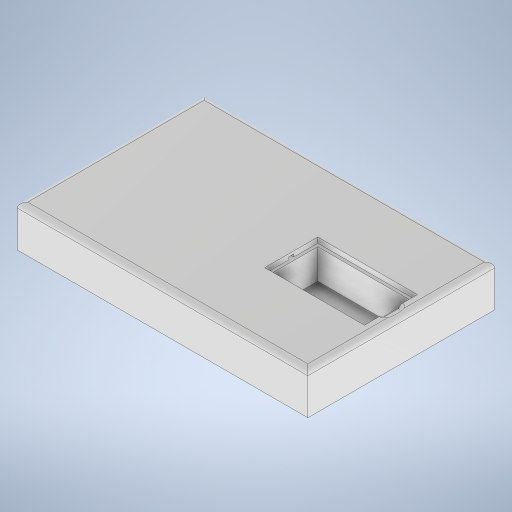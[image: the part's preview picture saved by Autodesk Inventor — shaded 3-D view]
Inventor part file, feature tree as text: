
AUTODESK INVENTOR PART (.ipt)
format: ipt  version: 2023 (Build 270158000, 158)  size: 339,456 bytes
history: native  units: in
note: dims shown in document units (in); Inventor stores cm internally (conversion verified against a paired STEP export)
features: extrude x7, sketch x3, fillet x2, shell x1
ambient origin geometry x8: Origin, YZ Plane, XZ Plane, XY Plane, X Axis, Y Axis, Z Axis, Center Point
bodies: Body1 (feature_tree)
feature tree (13):
  extrude  "Extrusion4"  Depth=4.5in
  extrude  "Extrusion7"  Depth=2.4in
  extrude  "Extrusion8"  Depth=1.125in
  fillet  "Fillet3"  Radius=2.25in
  extrude  "Extrusion11"  Depth=0.075in
  extrude  "Extrusion12"  Depth=0.075in
  fillet  "Fillet4"  Radius=1.6125in
  extrude  "Extrusion13"  Depth=0.25in
  shell  "Shell4"  Thickness=0.125in
  extrude  "Extrusion14"  Depth=0.25in TaperAngle=0.0deg
  sketch  "Sketch1"  dims[d0=7.0in d1=4.5in]
  sketch  "Sketch6"  dims[d32=1.0in d33=0.0in d34=2.4in]
  sketch  "Sketch7"  dims[d35=1.275in d36=1.125in d37=2.25in d38=0.075in d39=0.075in d41=1.6125in d42=0.25in d62=0.125in d63=0.0in d64=0.85in d65=0.0in d75=0.125in d82=1.6125in d83=0.375in d84=0.25in d85=0.5625in d86=1.0in d87=0.0in d88=0.0665in d89=0.0in d90=0.1in d91=0.0625in d92=0.0625in d93=0.0625in d94=0.1in d95=0.0in d96=0.2in d97=0.155in d98=0.155in d99=0.155in d100=0.155in d101=0.155in d102=0.155in d103=0.1in d104=0.1in d105=0.1in d106=0.1in d107=0.1in d108=0.1in d109=0.1in d110=0.1in d111=0.1in d112=0.1in d113=3.5in d114=3.5in d115=0.25in d116=0.0in]
